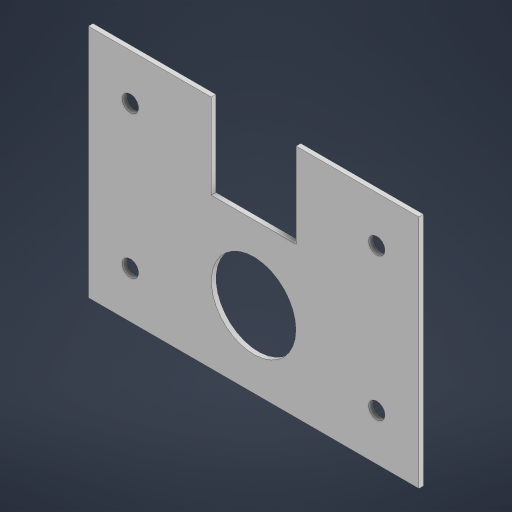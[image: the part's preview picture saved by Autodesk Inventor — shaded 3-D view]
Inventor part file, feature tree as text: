
AUTODESK INVENTOR PART (.ipt)
format: ipt  version: 2024 (Build 280153000, 153)  size: 184,832 bytes
history: native  units: in
note: dims shown in document units (in); Inventor stores cm internally (conversion verified against a paired STEP export)
features: sketch x2, extrude x1, hole x1, mirror x1
ambient origin geometry x8: Origin, YZ Plane, XZ Plane, XY Plane, X Axis, Y Axis, Z Axis, Center Point
bodies: Solid1 (feature_tree)
feature tree (5):
  extrude  "Extrusion1"  Depth=3.13in
  hole  "Hole1"  [1 undecoded]
  mirror  "Mirror1"
  sketch  "Sketch1"  dims[d0=4.4in d1=3.13in]
  sketch  "Sketch2"  dims[d2=1.13in d3=1.13in d4=1.01in d5=1.125in d6=0.0625in d7=0.0in d8=0.217in d9=0.75in d10=0.409in d11=0.25in d12=90.0deg d13=1.0in d14=0.8108in d15=1.9in d16=0.56in d17=0.56in d18=0.62in]
note: 1 required parameter value undecoded (feature->parameter linkage not recoverable at this tier; creation-order binding heuristic only, values carry confidence <= 0.55)
